# Revit family: Accessory-Tissue_Holder-KOHLER-ARTIFACTS-K-72576T
name_source: partatom
category: Specialty Equipment
revit_build: Autodesk Revit 2017 (Build: 20160225_1515(x64)
units: mm (PartAtom-declared; Revit-internal decimal feet)

## family parameters
Cut with Voids When Loaded = No
Host = Face
OmniClass Number = 23.31.25.21
OmniClass Title = Toilet Paper Dispensers
Part Type = Normal
Room Calculation Point = No
Round Connector Dimension = Use Diameter
Shared = No

## types (9) — shared parameters
ADA Compliant = No
Assembly Code = C1030200
Date Modified = 09/11/2020
Default Elevation = 42"
Description = Toilet paper holder (vertical type)
Height = 6 3/8"
Length = 6 3/4"
Manufacturer = KOHLER Co.
Master Format 2014 = 10 28 00
Master Format 2014 Name = Toilet, Bath, and Laundry Accessories
Material = Premium Metal Construction
Product Documentation Link = https://files.kohler.com.cn
Product Name = ARTIFACTS
Product Page URL = https://www.kohler.com.cn
URL = http://www.kohler.com.cn
WaterSense Certified = No
Width = 5 13/16"

## per-type parameters (varying)
| type | Finish | Model | Type |
| CP- Polished Chrome | Kohler-Metal-CP-Polished_Chrome | K-72576T-CP | 1 |
| AF- Flange Gold | Kohler-Metal-AF-Flange_Gold | K-72576T-AF | 2 |
| BN- Roman Silver | Kohler-Metal-BN-Roman_Silver | K-72576T-BN | 3 |
| BV- Roman Copper | Kohler-Metal-BV-Roman_Copper | K-72576T-BV | 4 |
| SN- Champagne gold | Kohler-Metal-SN-Champagne_Gold | K-72576T-SN | 5 |
| PGD- Eternal gold | Kohler-Metal-PGD-Eternal_Gold | K-72576T-PGD | 6 |
| RGD- Rose gold | Kohler-Metal-RGD-Rose_Gold | K-72576T-RGD | 7 |
| TT- Titanium Silver | Kohler-Metal-TT-Titanium_Silver | K-72576T-TT | 8 |
| 2BZ- Elegant black | Kohler-Metal-2BZ-Elegant_Black | K-72576T-2BZ | 9 |

## geometry (parser evidence)
native form markers: Sweep x4
no freeform markers — native parametric forms only
